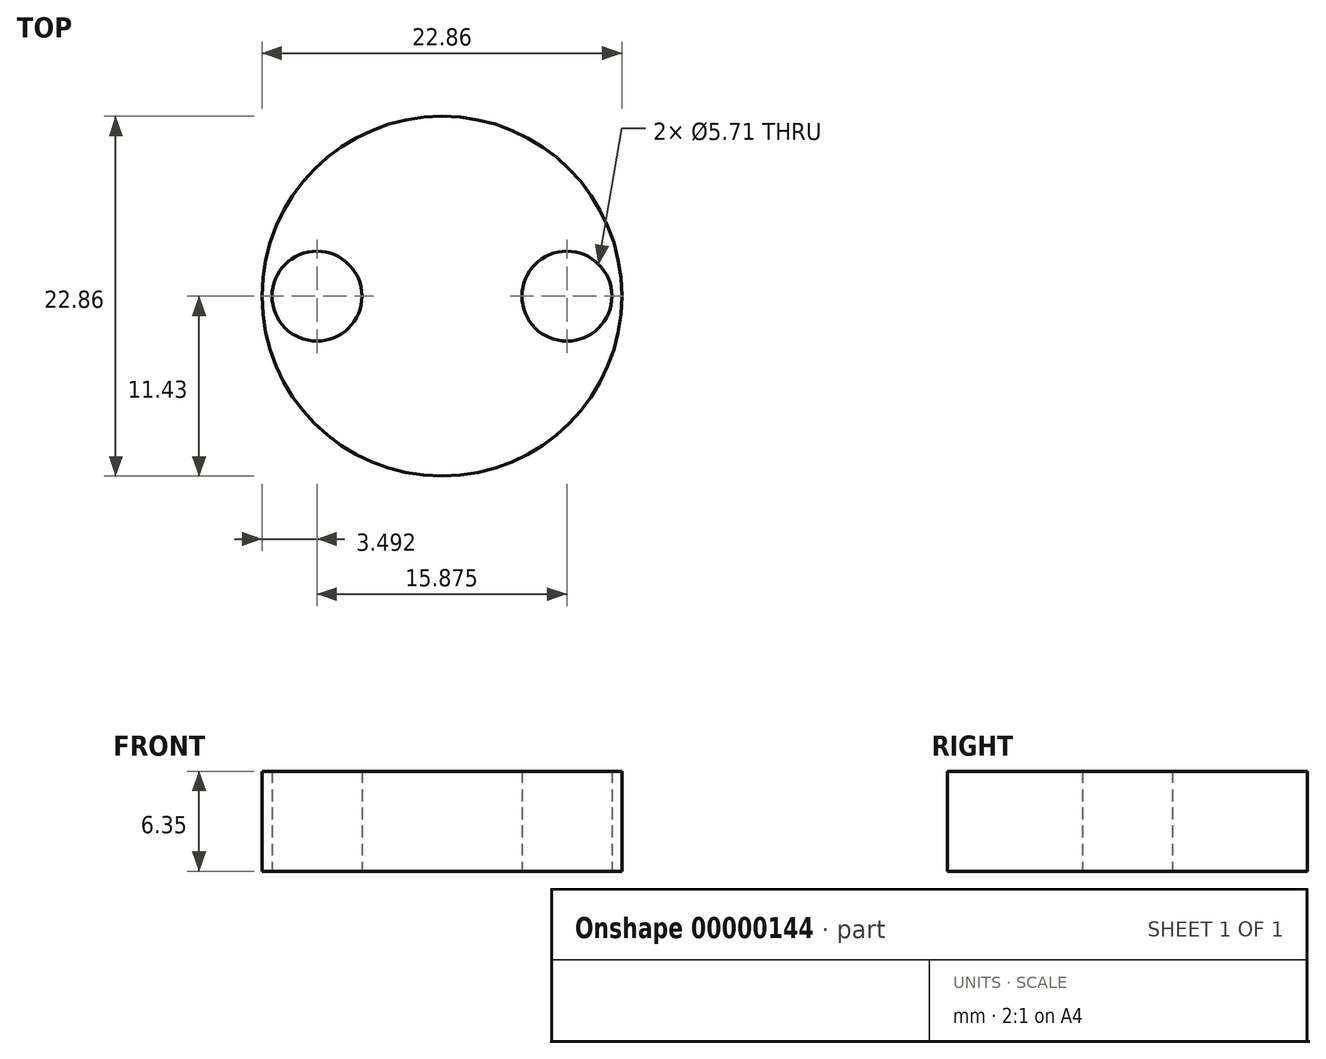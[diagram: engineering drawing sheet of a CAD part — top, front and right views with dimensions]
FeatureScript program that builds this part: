
annotation { "Feature Type Name" : "Feature", "Feature Type Description" : "" }
export const myFeature = defineFeature(function(context is Context, id is Id, definition is map)
    precondition{}
    {
        {
            var Q0;
            Q0=qCreatedBy(makeId("Top.planeOp"),FACE);
            var sketch = newSketch(context, id + "F0", { "sketchPlane" : qUnion([Q0])});
            skCircle(sketch, "E0", {"center": v(0, 0) * mm, "radius": 11.43 * mm});
            skCircle(sketch, "E1", {"center": v(7.94, 0) * mm, "radius": 2.86 * mm});
            skLineSegment(sketch, "E2", {"start": v(0, 0) * mm, "end": v(0, 11.43) * mm, "construction": true});
            skCircle(sketch, "E3.0.MirrorC", {"center": v(-7.94, 0) * mm, "radius": 2.86 * mm});
            skSolve(sketch);
        }
        {
            var Q0;
            Q0=makeQuery(id+"F0.imprint","IMPRINT",FACE,{"disambiguationData":[TD([[makeQuery(id+"F0.imprint","IMPRINT",EDGE,{"derivedFrom":sQuery(id+"F0.wireOp",EDGE,"E0")}),1.0]])]});
            extrude(context, id + "F1", {"entities" : qUnion([Q0]), "depth" : 6.35 * mm});
        }
    });
